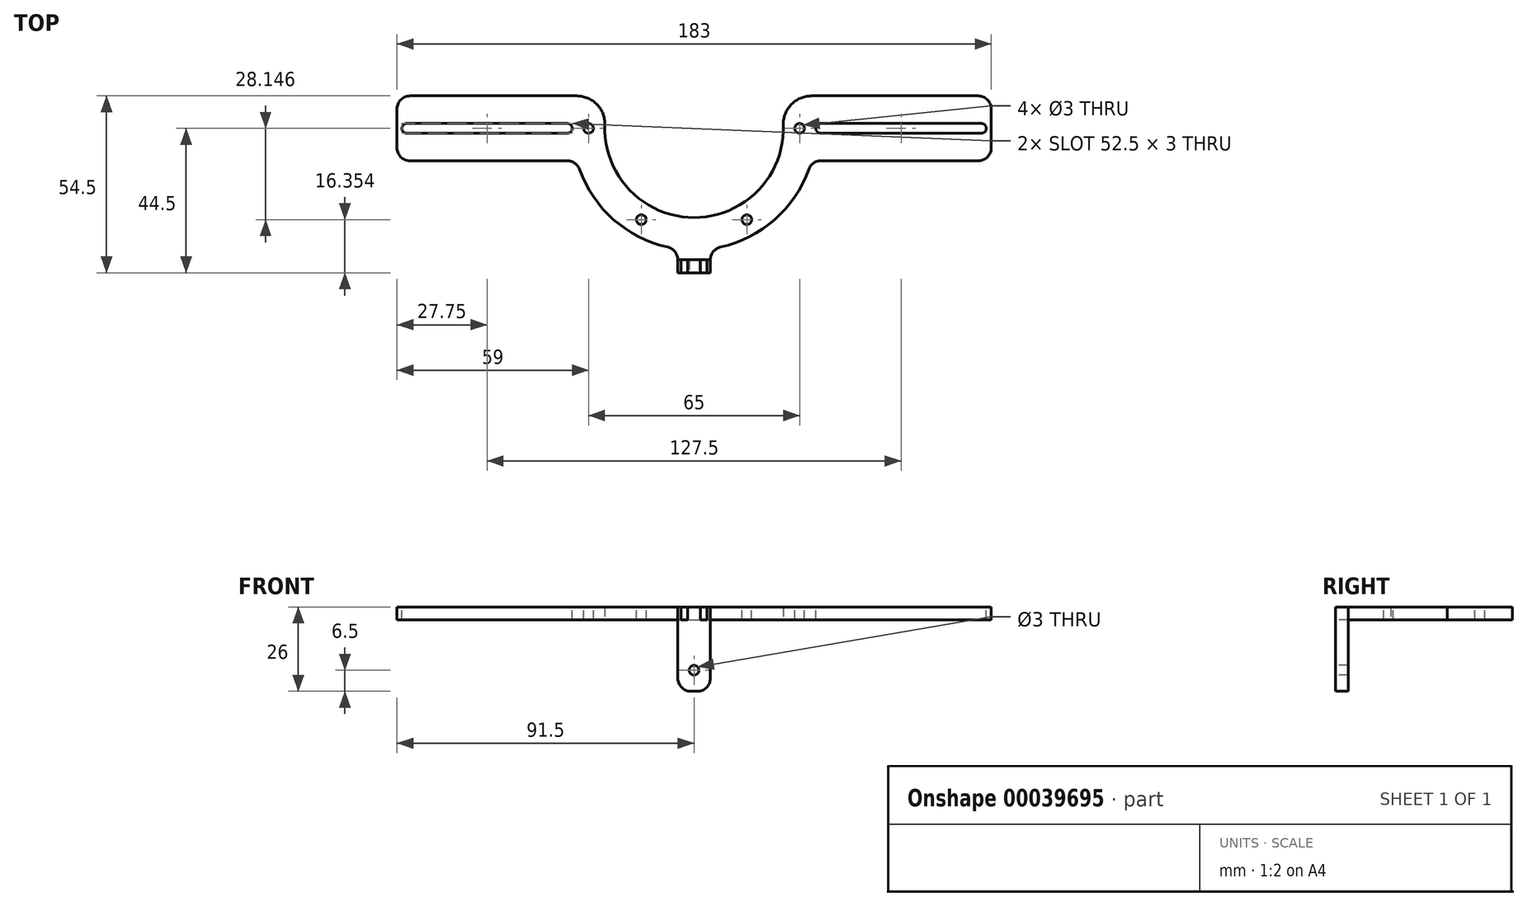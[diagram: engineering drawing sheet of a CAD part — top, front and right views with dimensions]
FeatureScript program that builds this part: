
annotation { "Feature Type Name" : "Feature", "Feature Type Description" : "" }
export const myFeature = defineFeature(function(context is Context, id is Id, definition is map)
    precondition{}
    {
        {
            var Q0;
            Q0=qCreatedBy(makeId("Top.planeOp"),FACE);
            var sketch = newSketch(context, id + "F0", { "sketchPlane" : qUnion([Q0])});
            skArc(sketch, "E0", {"start": v(-27.48, 1.01) * mm, "mid": v(0, -27.5) * mm, "end": v(27.48, 1.01) * mm});
            skLineSegment(sketch, "E1", {"start": v(36.14, 10) * mm, "end": v(91.5, 10) * mm});
            skLineSegment(sketch, "E2", {"start": v(91.5, 10) * mm, "end": v(91.5, -10) * mm});
            skLineSegment(sketch, "E3", {"start": v(91.5, -10) * mm, "end": v(36.14, -10) * mm});
            skLineSegment(sketch, "E4.MirrorCS", {"start": v(-36.14, 10) * mm, "end": v(-91.5, 10) * mm});
            skLineSegment(sketch, "E5.MirrorCS", {"start": v(-91.5, -10) * mm, "end": v(-36.14, -10) * mm});
            skLineSegment(sketch, "E6.MirrorCS", {"start": v(-91.5, 10) * mm, "end": v(-91.5, -10) * mm});
            skArc(sketch, "E7.trimOffspring", {"start": v(-36.14, -10) * mm, "mid": v(-24.65, -28.26) * mm, "end": v(-5, -37.17) * mm});
            skArc(sketch, "E8", {"start": v(-27.48, 1.01) * mm, "mid": v(-29.9, 7.35) * mm, "end": v(-36.14, 10) * mm});
            skArc(sketch, "E9.MirrorCS", {"start": v(27.48, 1.01) * mm, "mid": v(29.9, 7.35) * mm, "end": v(36.14, 10) * mm});
            skLineSegment(sketch, "E10.top", {"start": v(-5, -40.5) * mm, "end": v(-4, -40.5) * mm});
            skLineSegment(sketch, "E10.left", {"start": v(-5, -37.17) * mm, "end": v(-5, -40.5) * mm});
            skLineSegment(sketch, "E10.right", {"start": v(5, -37.17) * mm, "end": v(5, -40.5) * mm});
            skArc(sketch, "E11.trimOffspring", {"start": v(5, -37.17) * mm, "mid": v(24.65, -28.26) * mm, "end": v(36.14, -10) * mm});
            skLineSegment(sketch, "E12.top", {"start": v(4, -44.5) * mm, "end": v(2, -44.5) * mm});
            skLineSegment(sketch, "E12.left", {"start": v(4, -40.5) * mm, "end": v(4, -44.5) * mm});
            skLineSegment(sketch, "E12.right", {"start": v(2, -40.5) * mm, "end": v(2, -44.5) * mm});
            skLineSegment(sketch, "E13.trimOffspring", {"start": v(4, -40.5) * mm, "end": v(5, -40.5) * mm});
            skLineSegment(sketch, "E14.MirrorCS", {"start": v(-2, -40.5) * mm, "end": v(-2, -44.5) * mm});
            skLineSegment(sketch, "E15.MirrorCS", {"start": v(-4, -44.5) * mm, "end": v(-2, -44.5) * mm});
            skLineSegment(sketch, "E16.MirrorCS", {"start": v(-4, -40.5) * mm, "end": v(-4, -44.5) * mm});
            skLineSegment(sketch, "E17.trimOffspring", {"start": v(-2, -40.5) * mm, "end": v(2, -40.5) * mm});
            skSolve(sketch);
        }
        {
            var Q0;
            Q0=makeQuery(id+"F0.imprint","IMPRINT",FACE,{"disambiguationData":[TD([[makeQuery(id+"F0.imprint","IMPRINT",EDGE,{"derivedFrom":sQuery(id+"F0.wireOp",EDGE,"E0")}),-1.0]])]});
            extrude(context, id + "F1", {"entities" : qUnion([Q0]), "depth" : 4 * mm});
        }
        {
            var Q0;
            Q0=makeQuery(id+"F1.opExtrude","CAP_FACE",FACE,{"disambiguationData":[OSD([sQuery(id+"F0.wireOp",EDGE,"E0"),sQuery(id+"F0.wireOp",EDGE,"E1"),sQuery(id+"F0.wireOp",EDGE,"E2"),sQuery(id+"F0.wireOp",EDGE,"E3"),sQuery(id+"F0.wireOp",EDGE,"E4.MirrorCS"),sQuery(id+"F0.wireOp",EDGE,"E5.MirrorCS"),sQuery(id+"F0.wireOp",EDGE,"E6.MirrorCS"),sQuery(id+"F0.wireOp",EDGE,"E7.trimOffspring"),sQuery(id+"F0.wireOp",EDGE,"60a2d8de-b777-4c1f-a34a-a2666860c8b2.rect.bottom"),sQuery(id+"F0.wireOp",EDGE,"60a2d8de-b777-4c1f-a34a-a2666860c8b2.rect.left"),sQuery(id+"F0.wireOp",EDGE,"60a2d8de-b777-4c1f-a34a-a2666860c8b2.rect.right"),sQuery(id+"F0.wireOp",EDGE,"32dd4585-1418-4312-a656-0451d6199078.trimOffspring"),sQuery(id+"F0.wireOp",EDGE,"E8"),sQuery(id+"F0.wireOp",EDGE,"E9.MirrorCS")])],"isStart":false});
            var sketch = newSketch(context, id + "F2", { "sketchPlane" : qUnion([Q0])});
            skPoint(sketch, "E18", {"position": v(-32.5, 0) * mm});
            skPoint(sketch, "E19.center", {"position": v(0, 0) * mm});
            skLineSegment(sketch, "E19.anchor1", {"start": v(0, 0) * mm, "end": v(-32.5, 0) * mm, "construction": true});
            skPoint(sketch, "E20.1.0", {"position": v(-16.25, -28.15) * mm});
            skPoint(sketch, "E20.2.0", {"position": v(16.25, -28.15) * mm});
            skPoint(sketch, "E20.3.0", {"position": v(32.5, 0) * mm});
            skLineSegment(sketch, "E20.anchor2", {"start": v(0, 0) * mm, "end": v(32.5, 0) * mm, "construction": true});
            skSolve(sketch);
        }
        {
            var Q0;
            Q0=sQuery(id+"F2.wireOp",VERTEX,"E18");
            var Q1;
            Q1=sQuery(id+"F2.wireOp",VERTEX,"E20.1.0");
            var Q2;
            Q2=sQuery(id+"F2.wireOp",VERTEX,"E20.2.0");
            var Q3;
            Q3=sQuery(id+"F2.wireOp",VERTEX,"E20.3.0");
            var Q4;
            Q4=makeQuery(id+"F1.opExtrude","SWEPT_BODY",BODY,{"disambiguationData":[OSD([sQuery(id+"F0.wireOp",EDGE,"E0"),sQuery(id+"F0.wireOp",EDGE,"E1"),sQuery(id+"F0.wireOp",EDGE,"E2"),sQuery(id+"F0.wireOp",EDGE,"E3"),sQuery(id+"F0.wireOp",EDGE,"E4.MirrorCS"),sQuery(id+"F0.wireOp",EDGE,"E5.MirrorCS"),sQuery(id+"F0.wireOp",EDGE,"E6.MirrorCS"),sQuery(id+"F0.wireOp",EDGE,"E7.trimOffspring"),sQuery(id+"F0.wireOp",EDGE,"60a2d8de-b777-4c1f-a34a-a2666860c8b2.rect.bottom"),sQuery(id+"F0.wireOp",EDGE,"60a2d8de-b777-4c1f-a34a-a2666860c8b2.rect.left"),sQuery(id+"F0.wireOp",EDGE,"60a2d8de-b777-4c1f-a34a-a2666860c8b2.rect.right"),sQuery(id+"F0.wireOp",EDGE,"32dd4585-1418-4312-a656-0451d6199078.trimOffspring"),sQuery(id+"F0.wireOp",EDGE,"E8"),sQuery(id+"F0.wireOp",EDGE,"E9.MirrorCS")])]});
            hole(context, id + "F3", {"style" : HoleStyle.SIMPLE, "holeDiameter" : 3 * mm, "endStyle" : HoleEndStyle.THROUGH, "locations" : qUnion([Q0, Q1, Q2, Q3]), "scope" : qUnion([Q4])});
        }
        {
            var Q0;
            Q0=makeQuery(id+"F1.opExtrude","CAP_FACE",FACE,{"disambiguationData":[OSD([sQuery(id+"F0.wireOp",EDGE,"E0"),sQuery(id+"F0.wireOp",EDGE,"E1"),sQuery(id+"F0.wireOp",EDGE,"E2"),sQuery(id+"F0.wireOp",EDGE,"E3"),sQuery(id+"F0.wireOp",EDGE,"E4.MirrorCS"),sQuery(id+"F0.wireOp",EDGE,"E5.MirrorCS"),sQuery(id+"F0.wireOp",EDGE,"E6.MirrorCS"),sQuery(id+"F0.wireOp",EDGE,"E7.trimOffspring"),sQuery(id+"F0.wireOp",EDGE,"60a2d8de-b777-4c1f-a34a-a2666860c8b2.rect.bottom"),sQuery(id+"F0.wireOp",EDGE,"60a2d8de-b777-4c1f-a34a-a2666860c8b2.rect.left"),sQuery(id+"F0.wireOp",EDGE,"60a2d8de-b777-4c1f-a34a-a2666860c8b2.rect.right"),sQuery(id+"F0.wireOp",EDGE,"32dd4585-1418-4312-a656-0451d6199078.trimOffspring"),sQuery(id+"F0.wireOp",EDGE,"E8"),sQuery(id+"F0.wireOp",EDGE,"E9.MirrorCS")])],"isStart":false});
            var sketch = newSketch(context, id + "F4", { "sketchPlane" : qUnion([Q0])});
            skArc(sketch, "E21", {"start": v(-88.5, 1.5) * mm, "mid": v(-90, 0) * mm, "end": v(-88.5, -1.5) * mm});
            skArc(sketch, "E22", {"start": v(-39, -1.5) * mm, "mid": v(-37.5, 0) * mm, "end": v(-39, 1.5) * mm});
            skLineSegment(sketch, "E23", {"start": v(-88.5, 1.5) * mm, "end": v(-39, 1.5) * mm});
            skLineSegment(sketch, "E24", {"start": v(-88.5, -1.5) * mm, "end": v(-39, -1.5) * mm});
            skLineSegment(sketch, "E25.MirrorCS", {"start": v(88.5, -1.5) * mm, "end": v(39, -1.5) * mm});
            skArc(sketch, "E26.MirrorCS", {"start": v(88.5, 1.5) * mm, "mid": v(90, 0) * mm, "end": v(88.5, -1.5) * mm});
            skLineSegment(sketch, "E27.MirrorCS", {"start": v(88.5, 1.5) * mm, "end": v(39, 1.5) * mm});
            skArc(sketch, "E28.MirrorCS", {"start": v(39, -1.5) * mm, "mid": v(37.5, 0) * mm, "end": v(39, 1.5) * mm});
            skSolve(sketch);
        }
        {
            var Q0;
            Q0=makeQuery(id+"F4.imprint","IMPRINT",FACE,{"disambiguationData":[TD([[makeQuery(id+"F4.imprint","IMPRINT",EDGE,{"derivedFrom":sQuery(id+"F4.wireOp",EDGE,"E21")}),1.0]])]});
            var Q1;
            Q1=makeQuery(id+"F4.imprint","IMPRINT",FACE,{"disambiguationData":[TD([[makeQuery(id+"F4.imprint","IMPRINT",EDGE,{"derivedFrom":sQuery(id+"F4.wireOp",EDGE,"E25.MirrorCS")}),-1.0]])]});
            extrude(context, id + "F5", {"entities" : qUnion([Q0, Q1]), "operationType" : NewBodyOperationType.REMOVE, "endBound" : BoundingType.UP_TO_NEXT, "oppositeDirection" : true, "depth" : 25 * mm});
        }
        {
            var Q0;
            Q0=qCreatedBy(makeId("Right.planeOp"),FACE);
            var sketch = newSketch(context, id + "F6", { "sketchPlane" : qUnion([Q0])});
            skLineSegment(sketch, "E29", {"start": v(-40.5, 4) * mm, "end": v(-40.5, -22) * mm});
            skLineSegment(sketch, "E30", {"start": v(-40.5, -22) * mm, "end": v(-44.5, -22) * mm});
            skLineSegment(sketch, "E31", {"start": v(-44.5, -22) * mm, "end": v(-44.5, 4) * mm});
            skLineSegment(sketch, "E32", {"start": v(-40.5, 4) * mm, "end": v(-44.5, 4) * mm});
            skSolve(sketch);
        }
        {
            var Q0;
            Q0=makeQuery(id+"F6.imprint","IMPRINT",FACE,{"disambiguationData":[TD([[makeQuery(id+"F6.imprint","IMPRINT",EDGE,{"derivedFrom":sQuery(id+"F6.wireOp",EDGE,"b0b87136-15dc-40fc-8459-e5aed717f5bb")}),-1.0]])]});
            var Q1;
            Q1=makeQuery(id+"F6.imprint","IMPRINT",FACE,{"disambiguationData":[TD([[makeQuery(id+"F6.imprint","IMPRINT",EDGE,{"derivedFrom":sQuery(id+"F6.wireOp",EDGE,"E29")}),-1.0]])]});
            extrude(context, id + "F7", {"entities" : qUnion([Q0, Q1]), "depth" : 5 * mm, "hasSecondDirection" : true, "secondDirectionOppositeDirection" : true, "secondDirectionDepth" : 5 * mm});
        }
        {
            var Q0;
            Q0=makeQuery(id+"F1.opExtrude","SWEPT_EDGE",EDGE,{"disambiguationData":[OSD([sQuery(id+"F0.wireOp",EDGE,"E2"),sQuery(id+"F0.wireOp",EDGE,"E3")])]});
            var Q1;
            Q1=makeQuery(id+"F1.opExtrude","SWEPT_EDGE",EDGE,{"disambiguationData":[OSD([sQuery(id+"F0.wireOp",EDGE,"E3"),sQuery(id+"F0.wireOp",EDGE,"E7.trimOffspring")])]});
            var Q2;
            Q2=makeQuery(id+"F1.opExtrude","SWEPT_EDGE",EDGE,{"disambiguationData":[OSD([sQuery(id+"F0.wireOp",EDGE,"E5.MirrorCS"),sQuery(id+"F0.wireOp",EDGE,"E7.trimOffspring")])]});
            var Q3;
            Q3=makeQuery(id+"F1.opExtrude","SWEPT_EDGE",EDGE,{"disambiguationData":[OSD([sQuery(id+"F0.wireOp",EDGE,"E4.MirrorCS"),sQuery(id+"F0.wireOp",EDGE,"E8")])]});
            var Q4;
            Q4=makeQuery(id+"F1.opExtrude","SWEPT_EDGE",EDGE,{"disambiguationData":[OSD([sQuery(id+"F0.wireOp",EDGE,"E4.MirrorCS"),sQuery(id+"F0.wireOp",EDGE,"E6.MirrorCS")])]});
            var Q5;
            Q5=makeQuery(id+"F1.opExtrude","SWEPT_EDGE",EDGE,{"disambiguationData":[OSD([sQuery(id+"F0.wireOp",EDGE,"E5.MirrorCS"),sQuery(id+"F0.wireOp",EDGE,"E6.MirrorCS")])]});
            var Q6;
            Q6=makeQuery(id+"F1.opExtrude","SWEPT_EDGE",EDGE,{"disambiguationData":[OSD([sQuery(id+"F0.wireOp",EDGE,"E1"),sQuery(id+"F0.wireOp",EDGE,"E9.MirrorCS")])]});
            var Q7;
            Q7=makeQuery(id+"F1.opExtrude","SWEPT_EDGE",EDGE,{"disambiguationData":[OSD([sQuery(id+"F0.wireOp",EDGE,"E1"),sQuery(id+"F0.wireOp",EDGE,"E2")])]});
            var Q8;
            Q8=makeQuery(id+"F7.opExtrude","CAP_EDGE",EDGE,{"disambiguationData":[OSD([sQuery(id+"F6.wireOp",EDGE,"E30")])],"isStart":true});
            var Q9;
            Q9=makeQuery(id+"F7.opExtrude","CAP_EDGE",EDGE,{"disambiguationData":[OSD([sQuery(id+"F6.wireOp",EDGE,"E30")])],"isStart":false});
            var Q10;
            Q10=makeQuery(id+"F1.opExtrude","SWEPT_EDGE",EDGE,{"disambiguationData":[OSD([sQuery(id+"F0.wireOp",EDGE,"E10.right"),sQuery(id+"F0.wireOp",EDGE,"E11.trimOffspring")])]});
            fillet(context, id + "F8", {"entities" : qUnion([Q0, Q1, Q2, Q3, Q4, Q5, Q6, Q7, Q8, Q9, Q10]), "radius" : 4 * mm, "tangentPropagation" : true, "allowEdgeOverflow" : false});
        }
        {
            var Q0;
            Q0=makeQuery(id+"F7.opExtrude","SWEPT_FACE",FACE,{"disambiguationData":[OSD([sQuery(id+"F6.wireOp",EDGE,"E31")])]});
            var sketch = newSketch(context, id + "F9", { "sketchPlane" : qUnion([Q0])});
            skPoint(sketch, "E33", {"position": v(0, -15.5) * mm});
            skSolve(sketch);
        }
        {
            var Q0;
            Q0=sQuery(id+"F9.wireOp",VERTEX,"E33");
            var Q1;
            Q1=makeQuery(id+"F1.opExtrude","SWEPT_BODY",BODY,{"disambiguationData":[OSD([sQuery(id+"F0.wireOp",EDGE,"E0"),sQuery(id+"F0.wireOp",EDGE,"E1"),sQuery(id+"F0.wireOp",EDGE,"E2"),sQuery(id+"F0.wireOp",EDGE,"E3"),sQuery(id+"F0.wireOp",EDGE,"E4.MirrorCS"),sQuery(id+"F0.wireOp",EDGE,"E5.MirrorCS"),sQuery(id+"F0.wireOp",EDGE,"E6.MirrorCS"),sQuery(id+"F0.wireOp",EDGE,"E7.trimOffspring"),sQuery(id+"F0.wireOp",EDGE,"E8"),sQuery(id+"F0.wireOp",EDGE,"E9.MirrorCS")])]});
            var Q2;
            Q2=makeQuery(id+"F7.opExtrude","SWEPT_BODY",BODY,{"disambiguationData":[OSD([sQuery(id+"F6.wireOp",EDGE,"E29"),sQuery(id+"F6.wireOp",EDGE,"E30"),sQuery(id+"F6.wireOp",EDGE,"E31"),sQuery(id+"F6.wireOp",EDGE,"E32")])]});
            hole(context, id + "F10", {"style" : HoleStyle.SIMPLE, "holeDiameter" : 3 * mm, "endStyle" : HoleEndStyle.THROUGH, "locations" : qUnion([Q0]), "scope" : qUnion([Q1, Q2])});
        }
        {
            var Q0;
            Q0=makeQuery(id+"F7.opExtrude","SWEPT_FACE",FACE,{"disambiguationData":[OSD([sQuery(id+"F6.wireOp",EDGE,"E31")])]});
            var sketch = newSketch(context, id + "F11", { "sketchPlane" : qUnion([Q0])});
            skLineSegment(sketch, "E34.bottom", {"start": v(4, 4) * mm, "end": v(2, 4) * mm});
            skLineSegment(sketch, "E34.top", {"start": v(4, 0) * mm, "end": v(2, 0) * mm});
            skLineSegment(sketch, "E34.left", {"start": v(4, 4) * mm, "end": v(4, 0) * mm});
            skLineSegment(sketch, "E34.right", {"start": v(2, 4) * mm, "end": v(2, 0) * mm});
            skLineSegment(sketch, "E35.MirrorCS", {"start": v(-2, 4) * mm, "end": v(-2, 0) * mm});
            skLineSegment(sketch, "E36.MirrorCS", {"start": v(-4, 4) * mm, "end": v(-2, 4) * mm});
            skLineSegment(sketch, "E37.MirrorCS", {"start": v(-4, 4) * mm, "end": v(-4, 0) * mm});
            skLineSegment(sketch, "E38.MirrorCS", {"start": v(-4, 0) * mm, "end": v(-2, 0) * mm});
            skSolve(sketch);
        }
        {
            var Q0;
            Q0=makeQuery(id+"F11.imprint","IMPRINT",FACE,{"disambiguationData":[TD([[makeQuery(id+"F11.imprint","IMPRINT",EDGE,{"derivedFrom":sQuery(id+"F11.wireOp",EDGE,"E34.bottom")}),1.0]])]});
            var Q1;
            Q1=makeQuery(id+"F11.imprint","IMPRINT",FACE,{"disambiguationData":[TD([[makeQuery(id+"F11.imprint","IMPRINT",EDGE,{"derivedFrom":sQuery(id+"F11.wireOp",EDGE,"E35.MirrorCS")}),-1.0]])]});
            var Q2;
            Q2=makeQuery(id+"F7.opExtrude","SWEPT_FACE",FACE,{"disambiguationData":[OSD([sQuery(id+"F6.wireOp",EDGE,"E29")])]});
            extrude(context, id + "F12", {"entities" : qUnion([Q0, Q1]), "operationType" : NewBodyOperationType.REMOVE, "endBound" : BoundingType.UP_TO_SURFACE, "oppositeDirection" : true, "endBoundEntityFace" : qUnion([Q2]), "depth" : 25 * mm});
        }
    });
